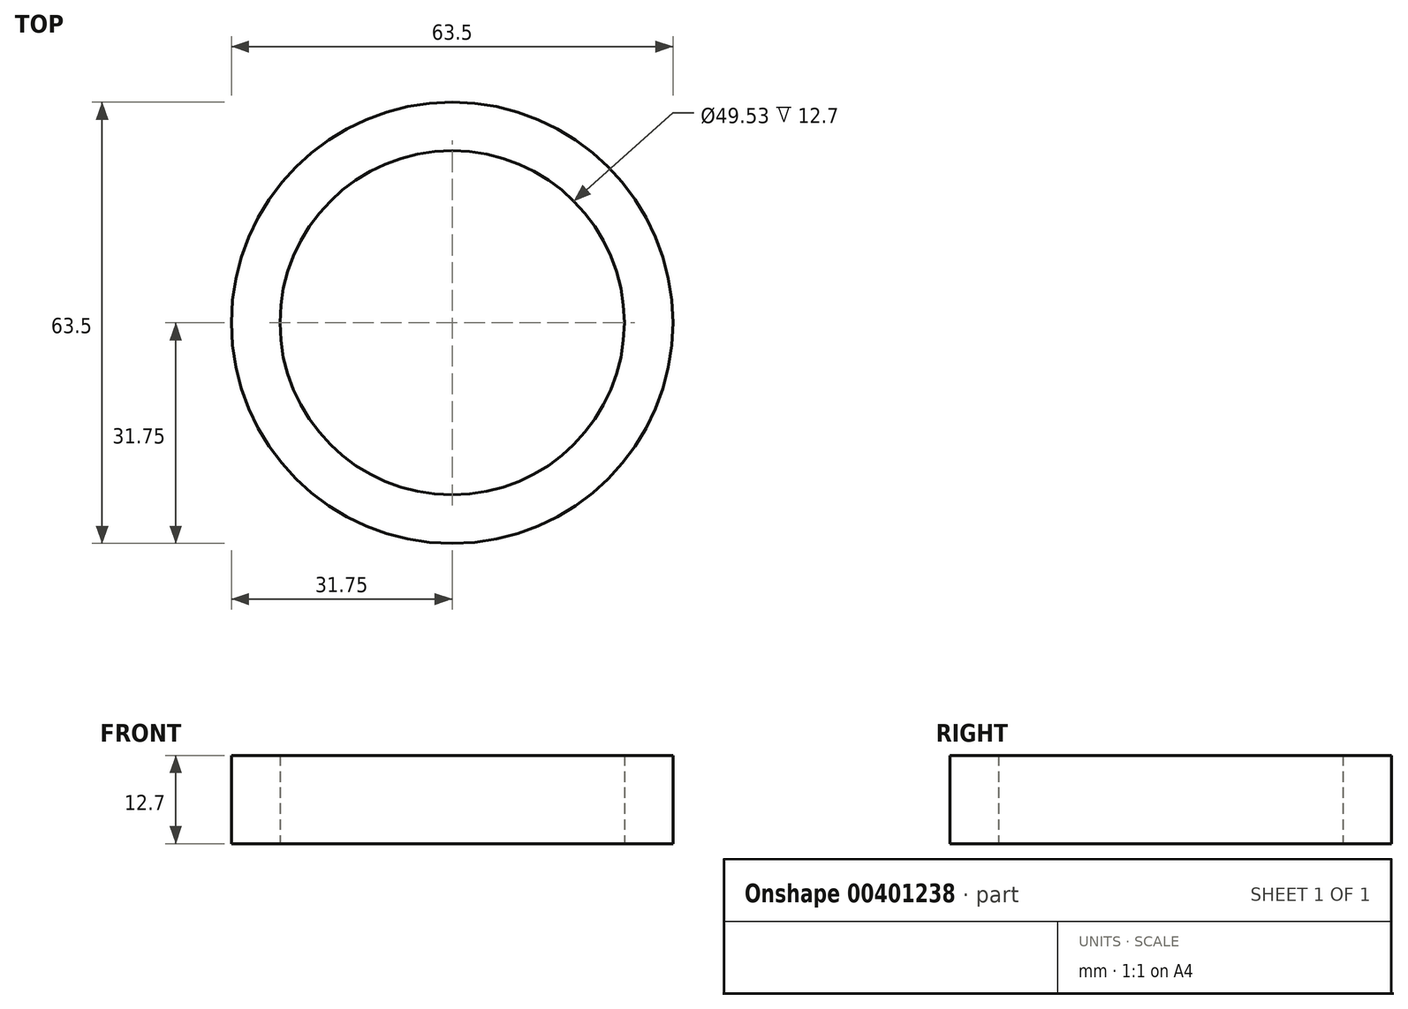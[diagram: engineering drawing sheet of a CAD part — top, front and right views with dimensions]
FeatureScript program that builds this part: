
annotation { "Feature Type Name" : "Feature", "Feature Type Description" : "" }
export const myFeature = defineFeature(function(context is Context, id is Id, definition is map)
    precondition{}
    {
        {
            var Q0;
            Q0=qCreatedBy(makeId("Top.planeOp"),FACE);
            var sketch = newSketch(context, id + "F0", { "sketchPlane" : qUnion([Q0])});
            skCircle(sketch, "E0", {"center": v(0, 0) * mm, "radius": 24.77 * mm});
            skCircle(sketch, "E1", {"center": v(0, 0) * mm, "radius": 31.75 * mm});
            skSolve(sketch);
        }
        {
            var Q0;
            Q0 = qSketchRegion(id + "F0", true);
            extrude(context, id + "F1", {"entities" : qUnion([Q0]), "depth" : 12.7 * mm});
        }
    });
